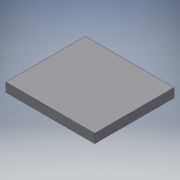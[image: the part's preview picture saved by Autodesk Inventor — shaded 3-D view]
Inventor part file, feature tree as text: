
AUTODESK INVENTOR PART (.ipt)
format: ipt  version: 2018 (Build 220112000, 112)  size: 90,112 bytes
history: native  units: mm
features: extrude x1, sketch x1
ambient origin geometry x8: Origin, YZ Plane, XZ Plane, XY Plane, X Axis, Y Axis, Z Axis, Center Point
bodies: Body1 (feature_tree)
feature tree (2):
  extrude  "Extrusão2"  Depth=125.0mm
  sketch  "Esboço2"  dims[d3=112.9mm d4=125.0mm d5=12.7mm d6=0.0mm]
